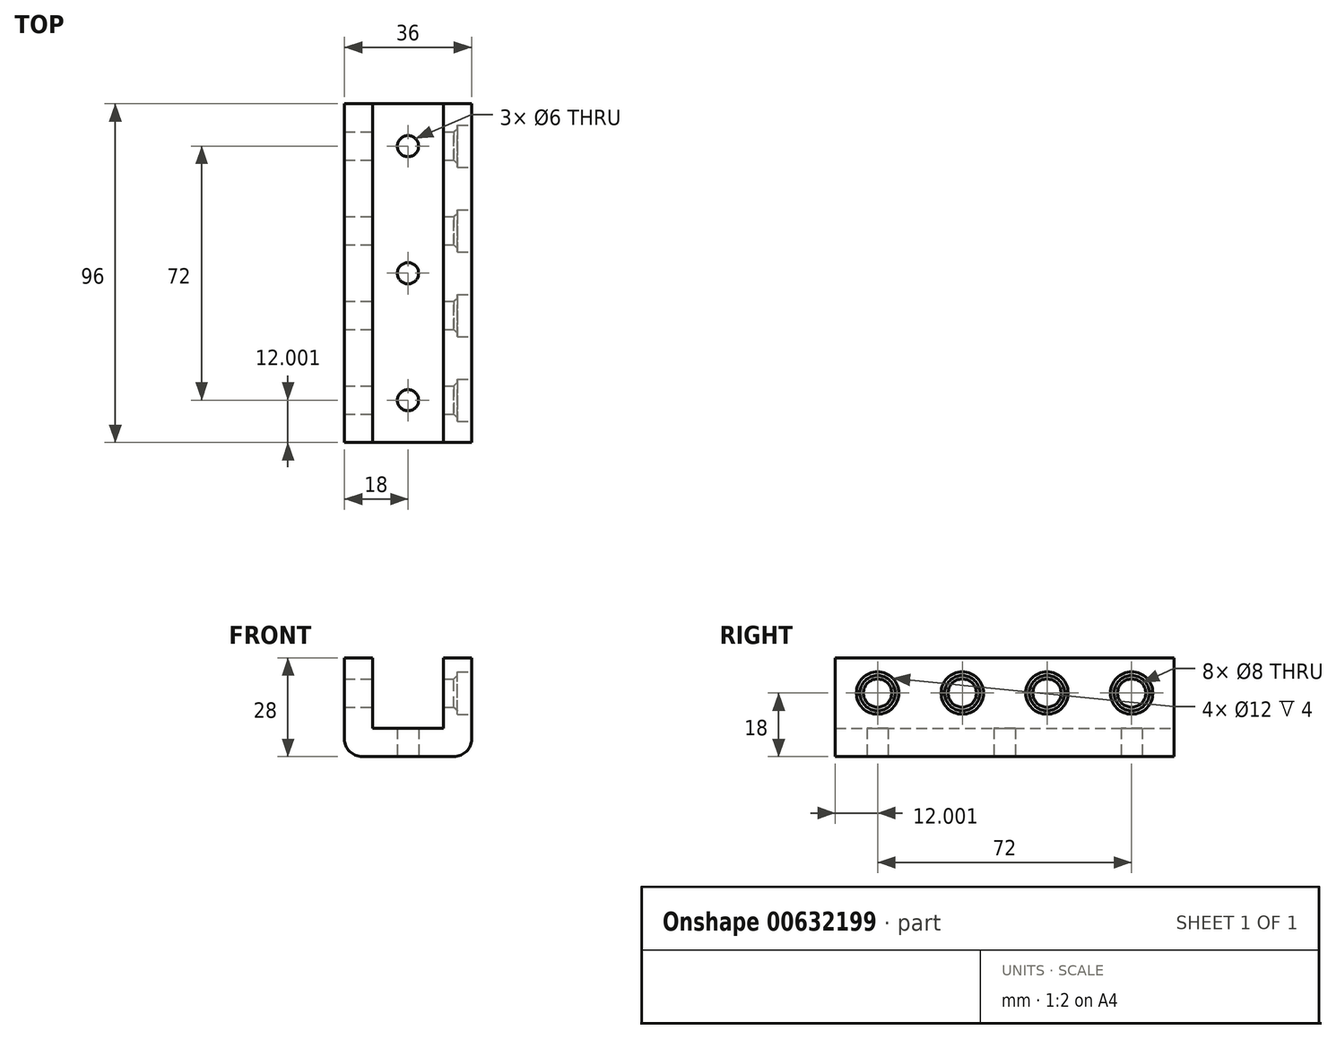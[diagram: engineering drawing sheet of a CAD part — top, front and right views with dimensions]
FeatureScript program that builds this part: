
annotation { "Feature Type Name" : "Feature", "Feature Type Description" : "" }
export const myFeature = defineFeature(function(context is Context, id is Id, definition is map)
    precondition{}
    {
        {
            var Q0;
            Q0=qCreatedBy(makeId("Right.planeOp"),FACE);
            var sketch = newSketch(context, id + "F0", { "sketchPlane" : qUnion([Q0])});
            skLineSegment(sketch, "E0.bottom", {"start": v(-37.15, -28) * mm, "end": v(58.85, -28) * mm});
            skLineSegment(sketch, "E0.top", {"start": v(-37.15, 0) * mm, "end": v(58.85, 0) * mm});
            skLineSegment(sketch, "E0.left", {"start": v(-37.15, -28) * mm, "end": v(-37.15, 0) * mm});
            skLineSegment(sketch, "E0.right", {"start": v(58.85, -28) * mm, "end": v(58.85, 0) * mm});
            skSolve(sketch);
        }
        {
            var Q0;
            Q0=makeQuery(id+"F0.imprint","IMPRINT",FACE,{"disambiguationData":[TD([[makeQuery(id+"F0.imprint","IMPRINT",EDGE,{"derivedFrom":sQuery(id+"F0.wireOp",EDGE,"E0.bottom")}),1.0]])]});
            extrude(context, id + "F1", {"entities" : qUnion([Q0]), "depth" : 36 * mm, "offsetDistance" : 25 * mm});
        }
        {
            var Q0;
            Q0=makeQuery(id+"F1.opExtrude","SWEPT_FACE",FACE,{"disambiguationData":[OSD([sQuery(id+"F0.wireOp",EDGE,"E0.top")])]});
            var sketch = newSketch(context, id + "F2", { "sketchPlane" : qUnion([Q0])});
            skLineSegment(sketch, "E1.bottom", {"start": v(8, -37.15) * mm, "end": v(28, -37.15) * mm});
            skLineSegment(sketch, "E1.top", {"start": v(8, 58.85) * mm, "end": v(28, 58.85) * mm});
            skLineSegment(sketch, "E1.left", {"start": v(8, -37.15) * mm, "end": v(8, 58.85) * mm});
            skLineSegment(sketch, "E1.right", {"start": v(28, -37.15) * mm, "end": v(28, 58.85) * mm});
            skSolve(sketch);
        }
        {
            var Q0;
            Q0=makeQuery(id+"F2.imprint","IMPRINT",FACE,{"disambiguationData":[TD([[makeQuery(id+"F2.imprint","IMPRINT",EDGE,{"derivedFrom":sQuery(id+"F2.wireOp",EDGE,"E1.bottom")}),-1.0]])]});
            extrude(context, id + "F3", {"entities" : qUnion([Q0]), "operationType" : NewBodyOperationType.REMOVE, "oppositeDirection" : true, "depth" : 20 * mm, "offsetDistance" : 25 * mm});
        }
        {
            var Q0;
            Q0=makeQuery(id+"F1.opExtrude","CAP_EDGE",EDGE,{"disambiguationData":[OSD([sQuery(id+"F0.wireOp",EDGE,"E0.bottom")])],"isStart":false});
            var Q1;
            Q1=makeQuery(id+"F1.opExtrude","CAP_EDGE",EDGE,{"disambiguationData":[OSD([sQuery(id+"F0.wireOp",EDGE,"E0.bottom")])],"isStart":true});
            fillet(context, id + "F4", {"entities" : qUnion([Q0, Q1]), "radius" : 5 * mm, "tangentPropagation" : true, "allowEdgeOverflow" : false});
        }
        {
            var Q0;
            Q0=makeQuery(id+"F1.opExtrude","CAP_FACE",FACE,{"disambiguationData":[OSD([sQuery(id+"F0.wireOp",EDGE,"E0.bottom"),sQuery(id+"F0.wireOp",EDGE,"E0.top"),sQuery(id+"F0.wireOp",EDGE,"E0.left"),sQuery(id+"F0.wireOp",EDGE,"E0.right")])],"isStart":false});
            var sketch = newSketch(context, id + "F5", { "sketchPlane" : qUnion([Q0])});
            skCircle(sketch, "E2", {"center": v(46.85, -10) * mm, "radius": 4 * mm});
            skCircle(sketch, "E3.1.0.0", {"center": v(22.85, -10) * mm, "radius": 4 * mm});
            skCircle(sketch, "E3.2.0.0", {"center": v(-1.15, -10) * mm, "radius": 4 * mm});
            skCircle(sketch, "E3.3.0.0", {"center": v(-25.15, -10) * mm, "radius": 4 * mm});
            skLineSegment(sketch, "E3.direction1", {"start": v(46.85, -10) * mm, "end": v(22.85, -10) * mm, "construction": true});
            skSolve(sketch);
        }
        {
            var Q0;
            Q0 = qSketchRegion(id + "F5", true);
            extrude(context, id + "F6", {"entities" : qUnion([Q0]), "operationType" : NewBodyOperationType.REMOVE, "oppositeDirection" : true, "depth" : 36 * mm, "offsetDistance" : 25 * mm});
        }
        {
            var Q0;
            Q0=makeQuery(id+"F1.opExtrude","CAP_FACE",FACE,{"disambiguationData":[OSD([sQuery(id+"F0.wireOp",EDGE,"E0.bottom"),sQuery(id+"F0.wireOp",EDGE,"E0.top"),sQuery(id+"F0.wireOp",EDGE,"E0.left"),sQuery(id+"F0.wireOp",EDGE,"E0.right")])],"isStart":false});
            var sketch = newSketch(context, id + "F7", { "sketchPlane" : qUnion([Q0])});
            skCircle(sketch, "E4", {"center": v(-25.15, -10) * mm, "radius": 6 * mm});
            skCircle(sketch, "E5.1.0.0", {"center": v(-1.15, -10) * mm, "radius": 6 * mm});
            skCircle(sketch, "E5.2.0.0", {"center": v(22.85, -10) * mm, "radius": 6 * mm});
            skCircle(sketch, "E5.3.0.0", {"center": v(46.85, -10) * mm, "radius": 6 * mm});
            skLineSegment(sketch, "E5.direction1", {"start": v(-25.15, -10) * mm, "end": v(-1.15, -10) * mm, "construction": true});
            skSolve(sketch);
        }
        {
            var Q0;
            Q0 = qSketchRegion(id + "F7", true);
            extrude(context, id + "F8", {"entities" : qUnion([Q0]), "operationType" : NewBodyOperationType.REMOVE, "oppositeDirection" : true, "depth" : 4 * mm, "offsetDistance" : 25 * mm});
        }
        {
            var Q0;
            Q0=makeQuery(id+"F8.boolean.opBoolean","INTERSECT",EDGE,{"derivedFrom":[makeQuery(id+"F6.boolean.opBoolean","COPY",FACE,{"disambiguationData":[TD([makeQuery(id+"F3.boolean.opBoolean","COPY",FACE,{"derivedFrom":makeQuery(id+"F3.opExtrude","SWEPT_FACE",FACE,{"disambiguationData":[OSD([sQuery(id+"F2.wireOp",EDGE,"E1.right")])]})})])],"derivedFrom":makeQuery(id+"F6.opExtrude","SWEPT_FACE",FACE,{"disambiguationData":[OSD([sQuery(id+"F5.wireOp",EDGE,"E3.3.0.0")])]})}),makeQuery(id+"F8.opExtrude","CAP_FACE",FACE,{"disambiguationData":[OSD([sQuery(id+"F7.wireOp",EDGE,"E4")])],"isStart":false})]});
            var Q1;
            Q1=makeQuery(id+"F8.boolean.opBoolean","INTERSECT",EDGE,{"derivedFrom":[makeQuery(id+"F6.boolean.opBoolean","COPY",FACE,{"disambiguationData":[TD([makeQuery(id+"F3.boolean.opBoolean","COPY",FACE,{"derivedFrom":makeQuery(id+"F3.opExtrude","SWEPT_FACE",FACE,{"disambiguationData":[OSD([sQuery(id+"F2.wireOp",EDGE,"E1.right")])]})})])],"derivedFrom":makeQuery(id+"F6.opExtrude","SWEPT_FACE",FACE,{"disambiguationData":[OSD([sQuery(id+"F5.wireOp",EDGE,"E3.2.0.0")])]})}),makeQuery(id+"F8.opExtrude","CAP_FACE",FACE,{"disambiguationData":[OSD([sQuery(id+"F7.wireOp",EDGE,"E5.1.0.0")])],"isStart":false})]});
            var Q2;
            Q2=makeQuery(id+"F8.boolean.opBoolean","INTERSECT",EDGE,{"derivedFrom":[makeQuery(id+"F6.boolean.opBoolean","COPY",FACE,{"disambiguationData":[TD([makeQuery(id+"F3.boolean.opBoolean","COPY",FACE,{"derivedFrom":makeQuery(id+"F3.opExtrude","SWEPT_FACE",FACE,{"disambiguationData":[OSD([sQuery(id+"F2.wireOp",EDGE,"E1.right")])]})})])],"derivedFrom":makeQuery(id+"F6.opExtrude","SWEPT_FACE",FACE,{"disambiguationData":[OSD([sQuery(id+"F5.wireOp",EDGE,"E3.1.0.0")])]})}),makeQuery(id+"F8.opExtrude","CAP_FACE",FACE,{"disambiguationData":[OSD([sQuery(id+"F7.wireOp",EDGE,"E5.2.0.0")])],"isStart":false})]});
            var Q3;
            Q3=makeQuery(id+"F8.boolean.opBoolean","INTERSECT",EDGE,{"derivedFrom":[makeQuery(id+"F6.boolean.opBoolean","COPY",FACE,{"disambiguationData":[TD([makeQuery(id+"F3.boolean.opBoolean","COPY",FACE,{"derivedFrom":makeQuery(id+"F3.opExtrude","SWEPT_FACE",FACE,{"disambiguationData":[OSD([sQuery(id+"F2.wireOp",EDGE,"E1.right")])]})})])],"derivedFrom":makeQuery(id+"F6.opExtrude","SWEPT_FACE",FACE,{"disambiguationData":[OSD([sQuery(id+"F5.wireOp",EDGE,"E2")])]})}),makeQuery(id+"F8.opExtrude","CAP_FACE",FACE,{"disambiguationData":[OSD([sQuery(id+"F7.wireOp",EDGE,"E5.3.0.0")])],"isStart":false})]});
            chamfer(context, id + "F9", {"entities" : qUnion([Q0, Q1, Q2, Q3]), "width" : 1 * mm, "tangentPropagation" : true});
        }
        {
            var Q0;
            Q0=makeQuery(id+"F1.opExtrude","SWEPT_FACE",FACE,{"disambiguationData":[OSD([sQuery(id+"F0.wireOp",EDGE,"E0.bottom")])]});
            var sketch = newSketch(context, id + "F10", { "sketchPlane" : qUnion([Q0])});
            skCircle(sketch, "E6", {"center": v(18, -46.85) * mm, "radius": 3 * mm});
            skPoint(sketch, "E6.centerSnap0", {"position": v(5, -10.85) * mm});
            skPoint(sketch, "E6.centerSnap1", {"position": v(18, 37.15) * mm});
            skCircle(sketch, "E7.0.1.0", {"center": v(18, -10.85) * mm, "radius": 3 * mm});
            skCircle(sketch, "E7.0.2.0", {"center": v(18, 25.15) * mm, "radius": 3 * mm});
            skLineSegment(sketch, "E7.direction1", {"start": v(18, -46.85) * mm, "end": v(43, -46.85) * mm, "construction": true});
            skLineSegment(sketch, "E7.direction2", {"start": v(18, -46.85) * mm, "end": v(18, -10.85) * mm, "construction": true});
            skSolve(sketch);
        }
        {
            var Q0;
            Q0 = qSketchRegion(id + "F10", true);
            extrude(context, id + "F11", {"entities" : qUnion([Q0]), "operationType" : NewBodyOperationType.REMOVE, "oppositeDirection" : true, "depth" : 8 * mm, "offsetDistance" : 25 * mm});
        }
    });
